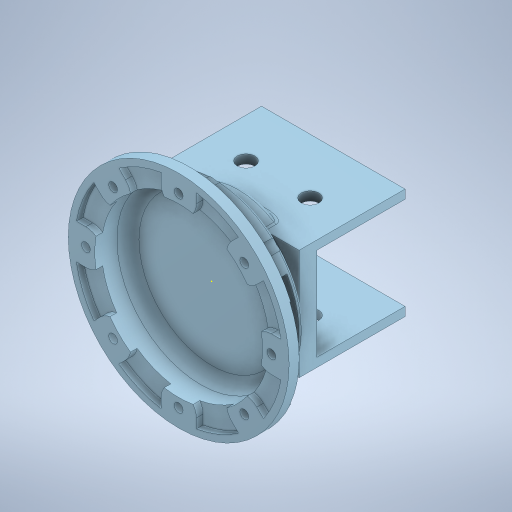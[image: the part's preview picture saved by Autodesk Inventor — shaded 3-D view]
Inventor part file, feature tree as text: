
AUTODESK INVENTOR PART (.ipt)
format: ipt  version: 2023.2 (Build 272271000, 271)  size: 622,592 bytes
history: native  units: in
note: dims shown in document units (in); Inventor stores cm internally (conversion verified against a paired STEP export)
features: sketch x8, extrude x8, projected_geometry x3, plane x1, other x1, fillet x1
ambient origin geometry x8: Origin, YZ Plane, XZ Plane, XY Plane, X Axis, Y Axis, Z Axis, Center Point
bodies: Solid1 (feature_tree), Body1 (feature_tree)
feature tree (22):
  sketch  "Boceto1"  dims[d0=1.9685in d1=0.9562in d2=0.0in]
  plane  "Plano de trabajo1"
  extrude  "Extrusión1"  Depth=0.9562in TaperAngle=0.0deg
  extrude  "Extrusión2"  Depth=0.1575in
  other  "Empalme de cara1"
  extrude  "Extrusión3"  Depth=0.3937in
  extrude  "Extrusión9"  Depth=0.8268in
  extrude  "Extrusión10"  Depth=0.1575in
  extrude  "Extrusión12"  Depth=0.7087in
  extrude  "Extrusión13"  Depth=0.315in
  fillet  "Empalme5"  Radius=2.5591in
  extrude  "Extrusión14"  Depth=0.3937in TaperAngle=0.0deg
  sketch  "Boceto2"  dims[d3=0.1575in d4=0.0in d5=0.1575in]
  sketch  "Boceto3"  dims[d6=0.3937in d7=0.0in d29=0.8268in]
  sketch  "Boceto4"  dims[d30=1.5748in d31=0.8268in]
  projected_geometry  "Contorno proyectado1"
  sketch  "Boceto10"  dims[d32=0.1181in d33=0.1575in]
  sketch  "Boceto12"  dims[d44=2.5591in d45=0.0in d46=0.7087in]
  sketch  "Boceto13"  dims[d47=0.7087in d48=0.315in d49=2.5591in d50=0.0in]
  projected_geometry  "Contorno proyectado3"
  projected_geometry  "Contorno proyectado4"
  sketch  "Boceto14"  dims[d54=0.3937in d55=0.0in d56=0.1969in d57=0.0in d58=0.0787in d59=0.2756in d60=0.2756in d61=0.2756in d62=0.2756in d63=0.2756in d64=0.2756in d65=0.2756in d66=0.5094in d67=0.0in d34=0.0197in d35=1.9685in d36=0.0197in d37=1.9685in]
